AUTODESK INVENTOR PART (.ipt)
format: ipt  version: 2018 (Build 220112000, 112)  size: 1,034,752 bytes
history: native  units: mm
features: sketch x15, revolve x2, extrude x2, pattern_circular x2, plane x2
ambient origin geometry x8: Origin, YZ Plane, XZ Plane, XY Plane, X Axis, Y Axis, Z Axis, Center Point
bodies: Solid1 (feature_tree)
feature tree (23):
  sketch  "Sketch1"  dims[d0=20.0mm d1=90.0deg]
  revolve  "Revolution1"  Angle=90.0deg
  sketch  "Sketch3"  dims[d5=20.0mm d6=0.0mm d7=60.0mm d8=360.0deg]
  sketch  "Sketch4"  dims[d10=800.0mm d11=20.0mm]
  extrude  "Extrusion1"  Depth=30.0mm
  pattern_circular  "Circular Pattern1"  Count=4  [1 undecoded]
  plane  "Work Plane1"
  sketch  "Sketch6"  dims[d14=25.0mm]
  sketch  "Sketch7"  dims[d15=30.0mm]
  revolve  "Revolution2"  Angle=360.0deg
  sketch  "Sketch9"  dims[d18=60.0mm d19=360.0deg]
  sketch  "Sketch10"
  sketch  "Sketch11"
  plane  "Work Plane2"
  sketch  "Sketch12"
  sketch  "Sketch13"
  extrude  "Extrusion2"  Depth=20.0mm
  pattern_circular  "Circular Pattern2"  Count=7  [1 undecoded]
  sketch  "Sketch15"
  sketch  "Sketch2"  dims[d2=30.0mm d3=30.0mm d4=40.0mm]
  sketch  "Sketch5"  dims[d12=90.0deg d13=70.0mm]
  sketch  "Sketch8"  dims[d16=5.0mm d17=0.0mm]
  sketch  "Sketch14"
note: 2 required parameter values undecoded (feature->parameter linkage not recoverable at this tier; creation-order binding heuristic only, values carry confidence <= 0.55)
